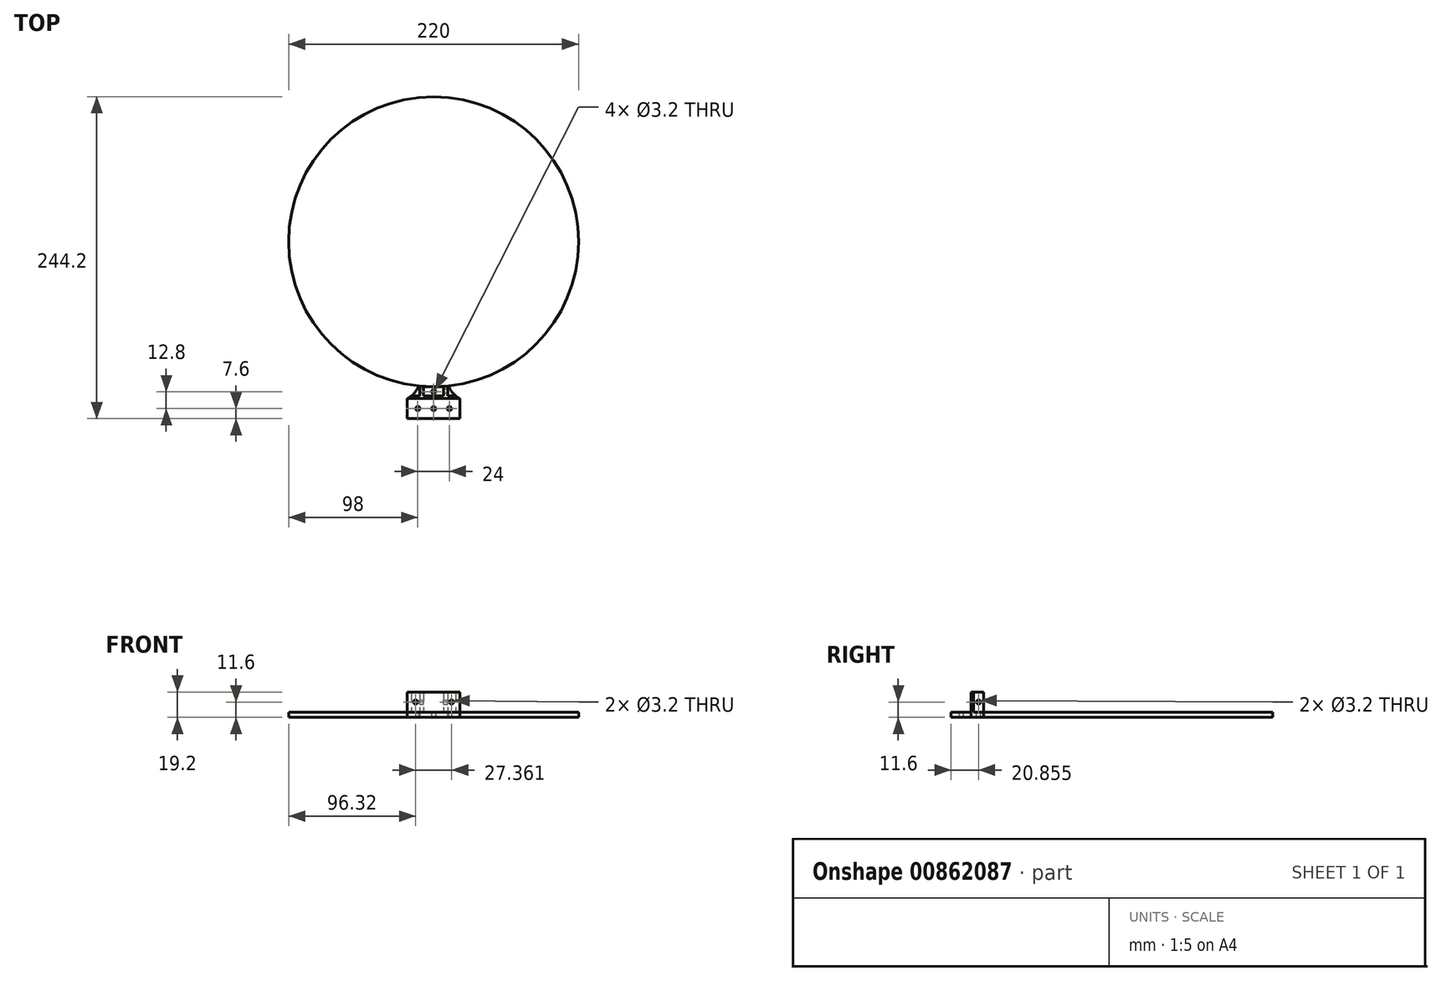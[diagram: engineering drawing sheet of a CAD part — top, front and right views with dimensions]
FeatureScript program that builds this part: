
annotation { "Feature Type Name" : "Feature", "Feature Type Description" : "" }
export const myFeature = defineFeature(function(context is Context, id is Id, definition is map)
    precondition{}
    {
        {
            assignVariable(context, id + "F0", {"name" : "Pad", "anyValue" : .2});
        }
        {
            var Q0;
            Q0=qCreatedBy(makeId("Top.planeOp"),FACE);
            var sketch = newSketch(context, id + "F1", { "sketchPlane" : qUnion([Q0])});
            skCircle(sketch, "E0", {"center": v(0, 0) * mm, "radius": 110 * mm});
            skCircle(sketch, "E1.0", {"center": v(0, 0) * mm, "radius": 110.2 * mm});
            skLineSegment(sketch, "E2", {"start": v(0, -110.2) * mm, "end": v(0, -119) * mm, "construction": true});
            skLineSegment(sketch, "E3", {"start": v(20, -119) * mm, "end": v(-20, -119) * mm});
            skLineSegment(sketch, "E4", {"start": v(-20, -119) * mm, "end": v(-20, -134.2) * mm});
            skLineSegment(sketch, "E5", {"start": v(-20, -134.2) * mm, "end": v(20, -134.2) * mm});
            skLineSegment(sketch, "E6", {"start": v(20, -134.2) * mm, "end": v(20, -119) * mm});
            skLineSegment(sketch, "E7", {"start": v(-11.5, -109.6) * mm, "end": v(11.5, -109.6) * mm});
            skPoint(sketch, "E8", {"position": v(0, -109.6) * mm});
            skLineSegment(sketch, "E9", {"start": v(-20, -119) * mm, "end": v(-11.5, -109.6) * mm, "construction": true});
            skLineSegment(sketch, "E10", {"start": v(11.5, -109.6) * mm, "end": v(20, -119) * mm, "construction": true});
            skLineSegment(sketch, "E11", {"start": v(-20, -126.6) * mm, "end": v(20, -126.6) * mm, "construction": true});
            skArc(sketch, "E12", {"start": v(-20, -119) * mm, "mid": v(-14.8, -115.16) * mm, "end": v(-11.5, -109.6) * mm});
            skArc(sketch, "E13", {"start": v(11.5, -109.6) * mm, "mid": v(14.8, -115.16) * mm, "end": v(20, -119) * mm});
            skCircle(sketch, "E14", {"center": v(0, -113.8) * mm, "radius": 1.6 * mm});
            skCircle(sketch, "E15", {"center": v(-12, -126.6) * mm, "radius": 1.6 * mm});
            skCircle(sketch, "E16", {"center": v(12, -126.6) * mm, "radius": 1.6 * mm});
            skCircle(sketch, "E17", {"center": v(0, -126.6) * mm, "radius": 1.6 * mm});
            skLineSegment(sketch, "E18", {"start": v(-7.6, -111.7) * mm, "end": v(7.6, -111.7) * mm, "construction": true});
            skPoint(sketch, "E19", {"position": v(0, -111.7) * mm});
            skLineSegment(sketch, "E20", {"start": v(-7.6, -109.6) * mm, "end": v(-7.6, -119) * mm});
            skLineSegment(sketch, "E21", {"start": v(7.6, -109.6) * mm, "end": v(7.6, -119) * mm});
            skLineSegment(sketch, "E22", {"start": v(-10.6, -109.6) * mm, "end": v(-10.6, -119) * mm});
            skLineSegment(sketch, "E23", {"start": v(10.6, -109.6) * mm, "end": v(10.6, -119) * mm});
            skLineSegment(sketch, "E24", {"start": v(-7.6, -117) * mm, "end": v(7.6, -117) * mm});
            skLineSegment(sketch, "E25", {"start": v(10.6, -117) * mm, "end": v(16.76, -117) * mm});
            skLineSegment(sketch, "E26", {"start": v(-10.6, -117) * mm, "end": v(-16.76, -117) * mm});
            skSolve(sketch);
        }
        {
            var Q0;
            Q0=makeQuery(id+"F1.imprint","IMPRINT",FACE,{"disambiguationData":[TD([[makeQuery(id+"F1.imprint","IMPRINT",EDGE,{"derivedFrom":sQuery(id+"F1.wireOp",EDGE,"E4")}),1.0]])]});
            extrude(context, id + "F2", {"entities" : qUnion([Q0]), "depth" : 4 * mm, "offsetDistance" : 25 * mm});
        }
        {
            var Q0;
            {var subQ4=sQuery(id+"F1.wireOp",EDGE,"E1.0");var subQ6=sQuery(id+"F1.wireOp",EDGE,"E22");var subQ8=makeQuery(id+"F1.imprint","INTERSECT",VERTEX,{"derivedFrom":[subQ4,subQ6]});Q0=makeQuery(id+"F1.imprint","IMPRINT",FACE,{"disambiguationData":[TD([[makeQuery(id+"F1.imprint","IMPRINT",EDGE,{"disambiguationData":[TD([[subQ8,-1.0]])],"derivedFrom":subQ4}),-1.0]])]});}
            var Q1;
            {var subQ5=sQuery(id+"F1.wireOp",EDGE,"E26");Q1=makeQuery(id+"F1.imprint","IMPRINT",FACE,{"disambiguationData":[TD([[makeQuery(id+"F1.imprint","IMPRINT",EDGE,{"derivedFrom":subQ5}),1.0]])]});}
            var Q2;
            {var subQ5=sQuery(id+"F1.wireOp",EDGE,"E24");Q2=makeQuery(id+"F1.imprint","IMPRINT",FACE,{"disambiguationData":[TD([[makeQuery(id+"F1.imprint","IMPRINT",EDGE,{"derivedFrom":subQ5}),-1.0]])]});}
            var Q3;
            {var subQ0=sQuery(id+"F1.wireOp",EDGE,"E21");var subQ2=sQuery(id+"F1.wireOp",EDGE,"E1.0");var subQ3=makeQuery(id+"F1.imprint","INTERSECT",VERTEX,{"derivedFrom":[subQ2,subQ0]});Q3=makeQuery(id+"F1.imprint","IMPRINT",FACE,{"disambiguationData":[TD([[makeQuery(id+"F1.imprint","IMPRINT",EDGE,{"disambiguationData":[TD([[subQ3,-1.0]])],"derivedFrom":subQ2}),-1.0]])]});}
            var Q4;
            {var subQ5=sQuery(id+"F1.wireOp",EDGE,"E25");Q4=makeQuery(id+"F1.imprint","IMPRINT",FACE,{"disambiguationData":[TD([[makeQuery(id+"F1.imprint","IMPRINT",EDGE,{"derivedFrom":subQ5}),-1.0]])]});}
            extrude(context, id + "F3", {"entities" : qUnion([Q0, Q1, Q2, Q3, Q4]), "operationType" : NewBodyOperationType.ADD, "depth" : (15 + 4 + getVariable(context, 'Pad')) * mm, "offsetDistance" : 25 * mm});
        }
        {
            var Q0;
            Q0=makeQuery(id+"F1.imprint","IMPRINT",FACE,{"disambiguationData":[TD([[makeQuery(id+"F1.imprint","IMPRINT",EDGE,{"derivedFrom":sQuery(id+"F1.wireOp",EDGE,"E14")}),-1.0]])]});
            var Q1;
            {var subQ5=sQuery(id+"F1.wireOp",EDGE,"E25");Q1=makeQuery(id+"F1.imprint","IMPRINT",FACE,{"disambiguationData":[TD([[makeQuery(id+"F1.imprint","IMPRINT",EDGE,{"derivedFrom":subQ5}),1.0]])]});}
            var Q2;
            {var subQ5=sQuery(id+"F1.wireOp",EDGE,"E26");Q2=makeQuery(id+"F1.imprint","IMPRINT",FACE,{"disambiguationData":[TD([[makeQuery(id+"F1.imprint","IMPRINT",EDGE,{"derivedFrom":subQ5}),-1.0]])]});}
            extrude(context, id + "F4", {"entities" : qUnion([Q0, Q1, Q2]), "operationType" : NewBodyOperationType.ADD, "depth" : 4 * mm, "offsetDistance" : 25 * mm});
        }
        {
            var Q0;
            Q0=makeQuery(id+"F3.opExtrude","SWEPT_FACE",FACE,{"disambiguationData":[OSD([sQuery(id+"F1.wireOp",EDGE,"E23")])]});
            var sketch = newSketch(context, id + "F5", { "sketchPlane" : qUnion([Q0])});
            skLineSegment(sketch, "E27.0", {"start": v(-117, 19.2) * mm, "end": v(-117, 4) * mm, "construction": true});
            skLineSegment(sketch, "E28", {"start": v(-117, 11.6) * mm, "end": v(-109.69, 11.6) * mm, "construction": true});
            skCircle(sketch, "E29", {"center": v(-113.34, 11.6) * mm, "radius": 1.6 * mm});
            skSolve(sketch);
        }
        {
            var Q0;
            Q0=makeQuery(id+"F5.imprint","IMPRINT",FACE,{"disambiguationData":[TD([[makeQuery(id+"F5.imprint","IMPRINT",EDGE,{"derivedFrom":sQuery(id+"F5.wireOp",EDGE,"W8VKcO90-A1dr-VWzd-Qr9l-NMxiFs6bawFf")}),1.0]])]});
            var Q1;
            Q1=makeQuery(id+"F5.imprint","IMPRINT",FACE,{"disambiguationData":[TD([[makeQuery(id+"F5.imprint","IMPRINT",EDGE,{"derivedFrom":sQuery(id+"F5.wireOp",EDGE,"E29")}),1.0]])]});
            extrude(context, id + "F6", {"entities" : qUnion([Q0, Q1]), "operationType" : NewBodyOperationType.REMOVE, "endBound" : BoundingType.THROUGH_ALL, "oppositeDirection" : true, "depth" : 25 * mm, "offsetDistance" : 25 * mm});
        }
        {
            var Q0;
            Q0=makeQuery(id+"F3.opExtrude","SWEPT_FACE",FACE,{"disambiguationData":[OSD([sQuery(id+"F1.wireOp",EDGE,"E26")])]});
            var sketch = newSketch(context, id + "F7", { "sketchPlane" : qUnion([Q0])});
            skLineSegment(sketch, "E30", {"start": v(-16.76, 11.6) * mm, "end": v(-10.6, 11.6) * mm, "construction": true});
            skLineSegment(sketch, "E31", {"start": v(10.6, 11.6) * mm, "end": v(16.76, 11.6) * mm, "construction": true});
            skCircle(sketch, "E32", {"center": v(13.68, 11.6) * mm, "radius": 1.6 * mm});
            skCircle(sketch, "E33", {"center": v(-13.68, 11.6) * mm, "radius": 1.6 * mm});
            skSolve(sketch);
        }
        {
            var Q0;
            Q0=makeQuery(id+"F7.imprint","IMPRINT",FACE,{"disambiguationData":[TD([[makeQuery(id+"F7.imprint","IMPRINT",EDGE,{"derivedFrom":sQuery(id+"F7.wireOp",EDGE,"E33")}),1.0]])]});
            var Q1;
            Q1=makeQuery(id+"F7.imprint","IMPRINT",FACE,{"disambiguationData":[TD([[makeQuery(id+"F7.imprint","IMPRINT",EDGE,{"derivedFrom":sQuery(id+"F7.wireOp",EDGE,"E32")}),1.0]])]});
            extrude(context, id + "F8", {"entities" : qUnion([Q0, Q1]), "operationType" : NewBodyOperationType.REMOVE, "endBound" : BoundingType.THROUGH_ALL, "oppositeDirection" : true, "depth" : 25 * mm, "offsetDistance" : 25 * mm});
        }
        {
            var Q0;
            {var subQ0=sQuery(id+"F1.wireOp",EDGE,"E7");var subQ1=sQuery(id+"F1.wireOp",EDGE,"E0");var subQ2=makeQuery(id+"F1.imprint","INTERSECT",VERTEX,{"disambiguationData":[OD(0.0)],"derivedFrom":[subQ1,subQ0]});Q0=makeQuery(id+"F1.imprint","IMPRINT",FACE,{"disambiguationData":[TD([[makeQuery(id+"F1.imprint","IMPRINT",EDGE,{"disambiguationData":[TD([[subQ2,1.0]])],"derivedFrom":subQ1}),1.0]])]});}
            var Q1;
            {var subQ0=sQuery(id+"F1.wireOp",EDGE,"E20");var subQ1=sQuery(id+"F1.wireOp",EDGE,"E0");var subQ2=makeQuery(id+"F1.imprint","INTERSECT",VERTEX,{"derivedFrom":[subQ1,subQ0]});Q1=makeQuery(id+"F1.imprint","IMPRINT",FACE,{"disambiguationData":[TD([[makeQuery(id+"F1.imprint","IMPRINT",EDGE,{"disambiguationData":[TD([[subQ2,-1.0]])],"derivedFrom":subQ1}),1.0]])]});}
            var Q2;
            {var subQ0=sQuery(id+"F1.wireOp",EDGE,"E20");var subQ1=sQuery(id+"F1.wireOp",EDGE,"E0");var subQ2=makeQuery(id+"F1.imprint","INTERSECT",VERTEX,{"derivedFrom":[subQ1,subQ0]});Q2=makeQuery(id+"F1.imprint","IMPRINT",FACE,{"disambiguationData":[TD([[makeQuery(id+"F1.imprint","IMPRINT",EDGE,{"disambiguationData":[TD([[subQ2,1.0]])],"derivedFrom":subQ1}),1.0]])]});}
            var Q3;
            {var subQ0=sQuery(id+"F1.wireOp",EDGE,"E21");var subQ1=sQuery(id+"F1.wireOp",EDGE,"E0");var subQ2=makeQuery(id+"F1.imprint","INTERSECT",VERTEX,{"derivedFrom":[subQ1,subQ0]});Q3=makeQuery(id+"F1.imprint","IMPRINT",FACE,{"disambiguationData":[TD([[makeQuery(id+"F1.imprint","IMPRINT",EDGE,{"disambiguationData":[TD([[subQ2,-1.0]])],"derivedFrom":subQ1}),1.0]])]});}
            extrude(context, id + "F9", {"entities" : qUnion([Q0, Q1, Q2, Q3]), "depth" : 4 * mm, "offsetDistance" : 25 * mm});
        }
    });
